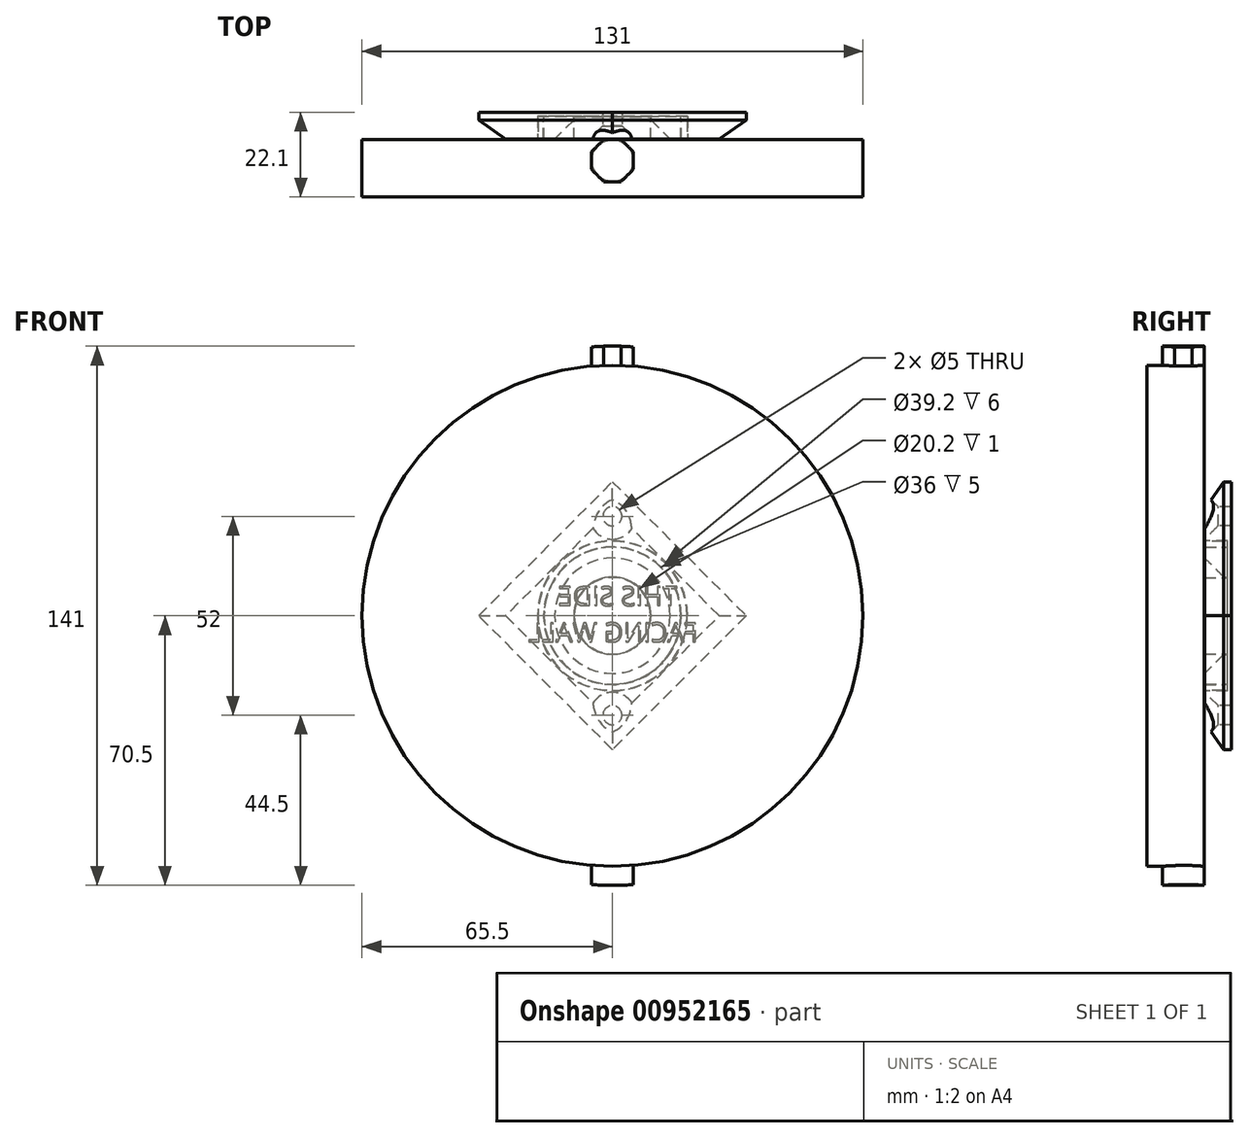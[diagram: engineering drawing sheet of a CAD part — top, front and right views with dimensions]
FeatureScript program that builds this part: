
annotation { "Feature Type Name" : "Feature", "Feature Type Description" : "" }
export const myFeature = defineFeature(function(context is Context, id is Id, definition is map)
    precondition{}
    {
        {
            var Q0;
            Q0=qCreatedBy(makeId("Front.planeOp"),FACE);
            var sketch = newSketch(context, id + "F0", { "sketchPlane" : qUnion([Q0])});
            skCircle(sketch, "E0", {"center": v(0, 0) * mm, "radius": 65.5 * mm});
            skCircle(sketch, "E1", {"center": v(0, 0) * mm, "radius": 19.5 * mm});
            skSolve(sketch);
        }
        {
            var Q0;
            Q0=makeQuery(id+"F0.imprint","IMPRINT",FACE,{"disambiguationData":[TD([[makeQuery(id+"F0.imprint","IMPRINT",EDGE,{"derivedFrom":sQuery(id+"F0.wireOp",EDGE,"E0")}),1.0]])]});
            var Q1;
            Q1=makeQuery(id+"F0.imprint","IMPRINT",FACE,{"disambiguationData":[TD([[makeQuery(id+"F0.imprint","IMPRINT",EDGE,{"derivedFrom":sQuery(id+"F0.wireOp",EDGE,"E1")}),1.0]])]});
            extrude(context, id + "F1", {"entities" : qUnion([Q0, Q1]), "depth" : 15 * mm, "offsetDistance" : 25 * mm});
        }
        {
            var Q0;
            Q0=makeQuery(id+"F0.imprint","IMPRINT",FACE,{"disambiguationData":[TD([[makeQuery(id+"F0.imprint","IMPRINT",EDGE,{"derivedFrom":sQuery(id+"F0.wireOp",EDGE,"E1")}),1.0]])]});
            var Q1;
            Q1=makeQuery(id+"F1.opExtrude","CAP_FACE",FACE,{"disambiguationData":[OSD([sQuery(id+"F0.wireOp",EDGE,"E0")])],"isStart":false});
            extrude(context, id + "F2", {"entities" : qUnion([Q0, Q1]), "operationType" : NewBodyOperationType.ADD, "oppositeDirection" : true, "depth" : 5 * mm, "offsetDistance" : 25 * mm});
        }
        {
            var Q0;
            Q0=qCreatedBy(makeId("Top.planeOp"),FACE);
            var sketch = newSketch(context, id + "F3", { "sketchPlane" : qUnion([Q0])});
            skCircle(sketch, "E2.cCircle", {"center": v(0, -5.5) * mm, "radius": 5.5 * mm, "construction": true});
            skLineSegment(sketch, "E2.0", {"start": v(-2.28, 0) * mm, "end": v(2.28, 0) * mm});
            skLineSegment(sketch, "E2.1", {"start": v(2.28, 0) * mm, "end": v(5.5, -3.22) * mm});
            skLineSegment(sketch, "E2.2", {"start": v(5.5, -3.22) * mm, "end": v(5.5, -7.78) * mm});
            skLineSegment(sketch, "E2.3", {"start": v(5.5, -7.78) * mm, "end": v(2.28, -11) * mm});
            skLineSegment(sketch, "E2.4", {"start": v(2.28, -11) * mm, "end": v(-2.28, -11) * mm});
            skLineSegment(sketch, "E2.5", {"start": v(-2.28, -11) * mm, "end": v(-5.5, -7.78) * mm});
            skLineSegment(sketch, "E2.6", {"start": v(-5.5, -7.78) * mm, "end": v(-5.5, -3.22) * mm});
            skLineSegment(sketch, "E2.7", {"start": v(-5.5, -3.22) * mm, "end": v(-2.28, 0) * mm});
            skPoint(sketch, "E2.0.midPoint", {"position": v(0, 0) * mm});
            skCircle(sketch, "E3", {"center": v(0, -5.5) * mm, "radius": 5.5 * mm});
            skSolve(sketch);
        }
        {
            var Q0;
            Q0 = qSketchRegion(id + "F3", true);
            var Q1;
            Q1=makeQuery(id+"F1.opExtrude","SWEPT_FACE",FACE,{"disambiguationData":[OSD([sQuery(id+"F0.wireOp",EDGE,"E0")])]});
            extrude(context, id + "F4", {"entities" : qUnion([Q0]), "operationType" : NewBodyOperationType.ADD, "endBound" : BoundingType.UP_TO_SURFACE, "depth" : 25 * mm, "endBoundEntityFace" : qUnion([Q1]), "hasOffset" : true, "offsetDistance" : -5 * mm});
        }
        {
            var Q0;
            Q0=qCreatedBy(makeId("Top.planeOp"),FACE);
            var sketch = newSketch(context, id + "F5", { "sketchPlane" : qUnion([Q0])});
            skCircle(sketch, "E4", {"center": v(0, -5.5) * mm, "radius": 5.5 * mm});
            skSolve(sketch);
        }
        {
            var Q0;
            Q0 = qSketchRegion(id + "F5", true);
            var Q1;
            Q1=makeQuery(id+"F1.opExtrude","SWEPT_FACE",FACE,{"disambiguationData":[OSD([sQuery(id+"F0.wireOp",EDGE,"E0")])]});
            extrude(context, id + "F6", {"entities" : qUnion([Q0]), "operationType" : NewBodyOperationType.ADD, "endBound" : BoundingType.UP_TO_SURFACE, "oppositeDirection" : true, "depth" : 25 * mm, "endBoundEntityFace" : qUnion([Q1]), "hasOffset" : true, "offsetDistance" : -5 * mm});
        }
        {
            var Q0;
            Q0=makeQuery(id+"F2.opExtrude","CAP_FACE",FACE,{"disambiguationData":[OSD([sQuery(id+"F0.wireOp",EDGE,"E1")])],"isStart":false});
            var sketch = newSketch(context, id + "F7", { "sketchPlane" : qUnion([Q0])});
            skCircle(sketch, "E5", {"center": v(0, 0) * mm, "radius": 18 * mm});
            skCircle(sketch, "E6", {"center": v(0, 0) * mm, "radius": 10 * mm});
            skSolve(sketch);
        }
        {
            var Q0;
            Q0=makeQuery(id+"F7.imprint","IMPRINT",FACE,{"disambiguationData":[TD([[makeQuery(id+"F7.imprint","IMPRINT",EDGE,{"derivedFrom":sQuery(id+"F7.wireOp",EDGE,"E5")}),1.0]])]});
            extrude(context, id + "F8", {"entities" : qUnion([Q0]), "operationType" : NewBodyOperationType.REMOVE, "oppositeDirection" : true, "depth" : 5 * mm, "offsetDistance" : 25 * mm});
        }
        {
            var Q0;
            Q0=makeQuery(id+"F8.boolean.opBoolean","SPLIT",FACE,{"disambiguationData":[TD([makeQuery(id+"F8.opExtrude","SWEPT_FACE",FACE,{"disambiguationData":[OSD([sQuery(id+"F7.wireOp",EDGE,"E6")])]})])],"derivedFrom":makeQuery(id+"F2.opExtrude","CAP_FACE",FACE,{"disambiguationData":[OSD([sQuery(id+"F0.wireOp",EDGE,"E1")])],"isStart":false})});
            extrude(context, id + "F9", {"entities" : qUnion([Q0]), "operationType" : NewBodyOperationType.ADD, "depth" : 1 * mm, "offsetDistance" : 25 * mm});
        }
        {
            var Q0;
            Q0=qCreatedBy(makeId("Front.planeOp"),FACE);
            var sketch = newSketch(context, id + "F10", { "sketchPlane" : qUnion([Q0])});
            skCircle(sketch, "E7.cCircle", {"center": v(0, 0) * mm, "radius": 35 * mm, "construction": true});
            skLineSegment(sketch, "E7.0", {"start": v(0, -35) * mm, "end": v(-35, 0) * mm});
            skLineSegment(sketch, "E7.1", {"start": v(-35, 0) * mm, "end": v(0, 35) * mm});
            skLineSegment(sketch, "E7.2", {"start": v(0, 35) * mm, "end": v(35, 0) * mm});
            skLineSegment(sketch, "E7.3", {"start": v(35, 0) * mm, "end": v(0, -35) * mm});
            skCircle(sketch, "E8", {"center": v(0, 26) * mm, "radius": 2.5 * mm});
            skCircle(sketch, "E9.MirrorC", {"center": v(0, -26) * mm, "radius": 2.5 * mm});
            skSolve(sketch);
        }
        {
            var Q0;
            Q0=makeQuery(id+"F10.imprint","IMPRINT",FACE,{"disambiguationData":[TD([[makeQuery(id+"F10.imprint","IMPRINT",EDGE,{"derivedFrom":sQuery(id+"F10.wireOp",EDGE,"E7.0")}),-1.0]])]});
            extrude(context, id + "F11", {"entities" : qUnion([Q0]), "oppositeDirection" : true, "depth" : 7 * mm, "offsetDistance" : 25 * mm});
        }
        {
            var Q0;
            Q0=makeQuery(id+"F1.opExtrude","SWEPT_BODY",BODY,{"disambiguationData":[OSD([sQuery(id+"F0.wireOp",EDGE,"E0")])]});
            var Q1;
            Q1=makeQuery(id+"F11.opExtrude","SWEPT_BODY",BODY,{"disambiguationData":[OSD([sQuery(id+"F10.wireOp",EDGE,"E7.0"),sQuery(id+"F10.wireOp",EDGE,"E7.1"),sQuery(id+"F10.wireOp",EDGE,"E7.2"),sQuery(id+"F10.wireOp",EDGE,"E7.3"),sQuery(id+"F10.wireOp",EDGE,"E8"),sQuery(id+"F10.wireOp",EDGE,"E9.MirrorC")])]});
            booleanBodies(context, id + "F12", {"operationType" : BooleanOperationType.SUBTRACTION, "tools" : qUnion([Q0]), "targets" : qUnion([Q1]), "offset" : true, "offsetAll" : true, "offsetDistance" : 0.1 * mm, "keepTools" : true});
        }
        {
            var Q0;
            Q0=makeQuery(id+"F12.tempBoolean.opBoolean","INTERSECT",EDGE,{"derivedFrom":[makeQuery(id+"F11.opExtrude","SWEPT_FACE",FACE,{"disambiguationData":[OSD([sQuery(id+"F10.wireOp",EDGE,"E8")])]}),makeQuery(id+"F12.offsetTempBody.opPattern","COPY",FACE,{"derivedFrom":makeQuery(id+"F4.boolean.opBoolean","MERGE",FACE,{"derivedFrom":[makeQuery(id+"F1.opExtrude","CAP_FACE",FACE,{"disambiguationData":[OSD([sQuery(id+"F0.wireOp",EDGE,"E0")])],"isStart":true}),makeQuery(id+"F4.opExtrude","SWEPT_FACE",FACE,{"disambiguationData":[OSD([sQuery(id+"F3.wireOp",EDGE,"E2.0")])]})]}),"instanceName":"1"})]});
            var Q1;
            Q1=makeQuery(id+"F12.tempBoolean.opBoolean","INTERSECT",EDGE,{"derivedFrom":[makeQuery(id+"F11.opExtrude","SWEPT_FACE",FACE,{"disambiguationData":[OSD([sQuery(id+"F10.wireOp",EDGE,"E9.MirrorC")])]}),makeQuery(id+"F12.offsetTempBody.opPattern","COPY",FACE,{"derivedFrom":makeQuery(id+"F4.boolean.opBoolean","MERGE",FACE,{"derivedFrom":[makeQuery(id+"F1.opExtrude","CAP_FACE",FACE,{"disambiguationData":[OSD([sQuery(id+"F0.wireOp",EDGE,"E0")])],"isStart":true}),makeQuery(id+"F4.opExtrude","SWEPT_FACE",FACE,{"disambiguationData":[OSD([sQuery(id+"F3.wireOp",EDGE,"E2.0")])]})]}),"instanceName":"1"})]});
            chamfer(context, id + "F13", {"entities" : qUnion([Q0, Q1]), "width" : 3.5 * mm, "tangentPropagation" : true});
        }
        {
            var Q0;
            Q0=makeQuery(id+"F12.tempBoolean.opBoolean","INTERSECT",EDGE,{"derivedFrom":[makeQuery(id+"F11.opExtrude","SWEPT_FACE",FACE,{"disambiguationData":[OSD([sQuery(id+"F10.wireOp",EDGE,"E7.0")])]}),makeQuery(id+"F12.offsetTempBody.opPattern","COPY",FACE,{"derivedFrom":makeQuery(id+"F4.boolean.opBoolean","MERGE",FACE,{"derivedFrom":[makeQuery(id+"F1.opExtrude","CAP_FACE",FACE,{"disambiguationData":[OSD([sQuery(id+"F0.wireOp",EDGE,"E0")])],"isStart":true}),makeQuery(id+"F4.opExtrude","SWEPT_FACE",FACE,{"disambiguationData":[OSD([sQuery(id+"F3.wireOp",EDGE,"E2.0")])]})]}),"instanceName":"1"})]});
            var Q1;
            Q1=makeQuery(id+"F12.tempBoolean.opBoolean","INTERSECT",EDGE,{"derivedFrom":[makeQuery(id+"F11.opExtrude","SWEPT_FACE",FACE,{"disambiguationData":[OSD([sQuery(id+"F10.wireOp",EDGE,"E7.1")])]}),makeQuery(id+"F12.offsetTempBody.opPattern","COPY",FACE,{"derivedFrom":makeQuery(id+"F4.boolean.opBoolean","MERGE",FACE,{"derivedFrom":[makeQuery(id+"F1.opExtrude","CAP_FACE",FACE,{"disambiguationData":[OSD([sQuery(id+"F0.wireOp",EDGE,"E0")])],"isStart":true}),makeQuery(id+"F4.opExtrude","SWEPT_FACE",FACE,{"disambiguationData":[OSD([sQuery(id+"F3.wireOp",EDGE,"E2.0")])]})]}),"instanceName":"1"})]});
            var Q2;
            Q2=makeQuery(id+"F12.tempBoolean.opBoolean","INTERSECT",EDGE,{"derivedFrom":[makeQuery(id+"F11.opExtrude","SWEPT_FACE",FACE,{"disambiguationData":[OSD([sQuery(id+"F10.wireOp",EDGE,"E7.2")])]}),makeQuery(id+"F12.offsetTempBody.opPattern","COPY",FACE,{"derivedFrom":makeQuery(id+"F4.boolean.opBoolean","MERGE",FACE,{"derivedFrom":[makeQuery(id+"F1.opExtrude","CAP_FACE",FACE,{"disambiguationData":[OSD([sQuery(id+"F0.wireOp",EDGE,"E0")])],"isStart":true}),makeQuery(id+"F4.opExtrude","SWEPT_FACE",FACE,{"disambiguationData":[OSD([sQuery(id+"F3.wireOp",EDGE,"E2.0")])]})]}),"instanceName":"1"})]});
            var Q3;
            Q3=makeQuery(id+"F12.tempBoolean.opBoolean","INTERSECT",EDGE,{"derivedFrom":[makeQuery(id+"F11.opExtrude","SWEPT_FACE",FACE,{"disambiguationData":[OSD([sQuery(id+"F10.wireOp",EDGE,"E7.3")])]}),makeQuery(id+"F12.offsetTempBody.opPattern","COPY",FACE,{"derivedFrom":makeQuery(id+"F4.boolean.opBoolean","MERGE",FACE,{"derivedFrom":[makeQuery(id+"F1.opExtrude","CAP_FACE",FACE,{"disambiguationData":[OSD([sQuery(id+"F0.wireOp",EDGE,"E0")])],"isStart":true}),makeQuery(id+"F4.opExtrude","SWEPT_FACE",FACE,{"disambiguationData":[OSD([sQuery(id+"F3.wireOp",EDGE,"E2.0")])]})]}),"instanceName":"1"})]});
            var Q4;
            Q4=makeQuery(id+"F12.tempBoolean.opBoolean","COPY",EDGE,{"derivedFrom":makeQuery(id+"F12.offsetTempBody.opPattern","COPY",EDGE,{"derivedFrom":makeQuery(id+"F8.boolean.opBoolean","COPY",EDGE,{"derivedFrom":makeQuery(id+"F8.opExtrude","CAP_EDGE",EDGE,{"disambiguationData":[OSD([sQuery(id+"F7.wireOp",EDGE,"E6")])],"isStart":false})}),"instanceName":"1"})});
            chamfer(context, id + "F14", {"entities" : qUnion([Q0, Q1, Q2, Q3, Q4]), "width" : 5 * mm, "tangentPropagation" : true});
        }
        {
            var Q0;
            Q0=makeQuery(id+"F11.opExtrude","CAP_FACE",FACE,{"disambiguationData":[OSD([sQuery(id+"F10.wireOp",EDGE,"E7.0"),sQuery(id+"F10.wireOp",EDGE,"E7.1"),sQuery(id+"F10.wireOp",EDGE,"E7.2"),sQuery(id+"F10.wireOp",EDGE,"E7.3"),sQuery(id+"F10.wireOp",EDGE,"E8"),sQuery(id+"F10.wireOp",EDGE,"E9.MirrorC")])],"isStart":false});
            var sketch = newSketch(context, id + "F15", { "sketchPlane" : qUnion([Q0])});
            skText(sketch, "E10", { "text": "   THIS SIDE\nFACING WALL", "fontName": "OpenSans-Regular.ttf"});
            const initialGuessF15  = {"E10": [-0.02236, 0.00264, 1, 0, 0.005]};
            skSetInitialGuess(sketch, initialGuessF15);
            skSolve(sketch);
        }
        {
            var Q0;
            Q0=makeQuery(id+"F15.imprint","IMPRINT",FACE,{"disambiguationData":[TD([[makeQuery(id+"F15.imprint","IMPRINT",EDGE,{"derivedFrom":sQuery(id+"F15.wireOp",EDGE,"E10.sketch_text.stroke-0")}),1.0]])]});
            var Q1;
            Q1=makeQuery(id+"F15.imprint","IMPRINT",FACE,{"disambiguationData":[TD([[makeQuery(id+"F15.imprint","IMPRINT",EDGE,{"derivedFrom":sQuery(id+"F15.wireOp",EDGE,"E10.sketch_text.stroke-122")}),1.0]])]});
            var Q2;
            Q2=makeQuery(id+"F15.imprint","IMPRINT",FACE,{"disambiguationData":[TD([[makeQuery(id+"F15.imprint","IMPRINT",EDGE,{"derivedFrom":sQuery(id+"F15.wireOp",EDGE,"E10.sketch_text.stroke-85")}),1.0]])]});
            var Q3;
            Q3=makeQuery(id+"F15.imprint","IMPRINT",FACE,{"disambiguationData":[TD([[makeQuery(id+"F15.imprint","IMPRINT",EDGE,{"derivedFrom":sQuery(id+"F15.wireOp",EDGE,"E10.sketch_text.stroke-209")}),1.0]])]});
            extrude(context, id + "F16", {"entities" : qUnion([Q0, Q1, Q2, Q3]), "operationType" : NewBodyOperationType.ADD, "depth" : .1 * mm, "offsetDistance" : 25 * mm});
        }
        {
            var Q0;
            {var subQ0=sQuery(id+"F0.wireOp",EDGE,"E1");Q0=makeQuery(id+"F12.tempBoolean.opBoolean","COPY",FACE,{"derivedFrom":makeQuery(id+"F12.offsetTempBody.opPattern","COPY",FACE,{"derivedFrom":makeQuery(id+"F8.boolean.opBoolean","SPLIT",FACE,{"disambiguationData":[TD([makeQuery(id+"F2.opExtrude","SWEPT_FACE",FACE,{"disambiguationData":[OSD([subQ0])]})])],"derivedFrom":makeQuery(id+"F2.opExtrude","CAP_FACE",FACE,{"disambiguationData":[OSD([subQ0])],"isStart":false})}),"instanceName":"1"})});}
            extrude(context, id + "F17", {"entities" : qUnion([Q0]), "operationType" : NewBodyOperationType.REMOVE, "oppositeDirection" : true, "depth" : 1 * mm, "offsetDistance" : 25 * mm});
        }
    });
